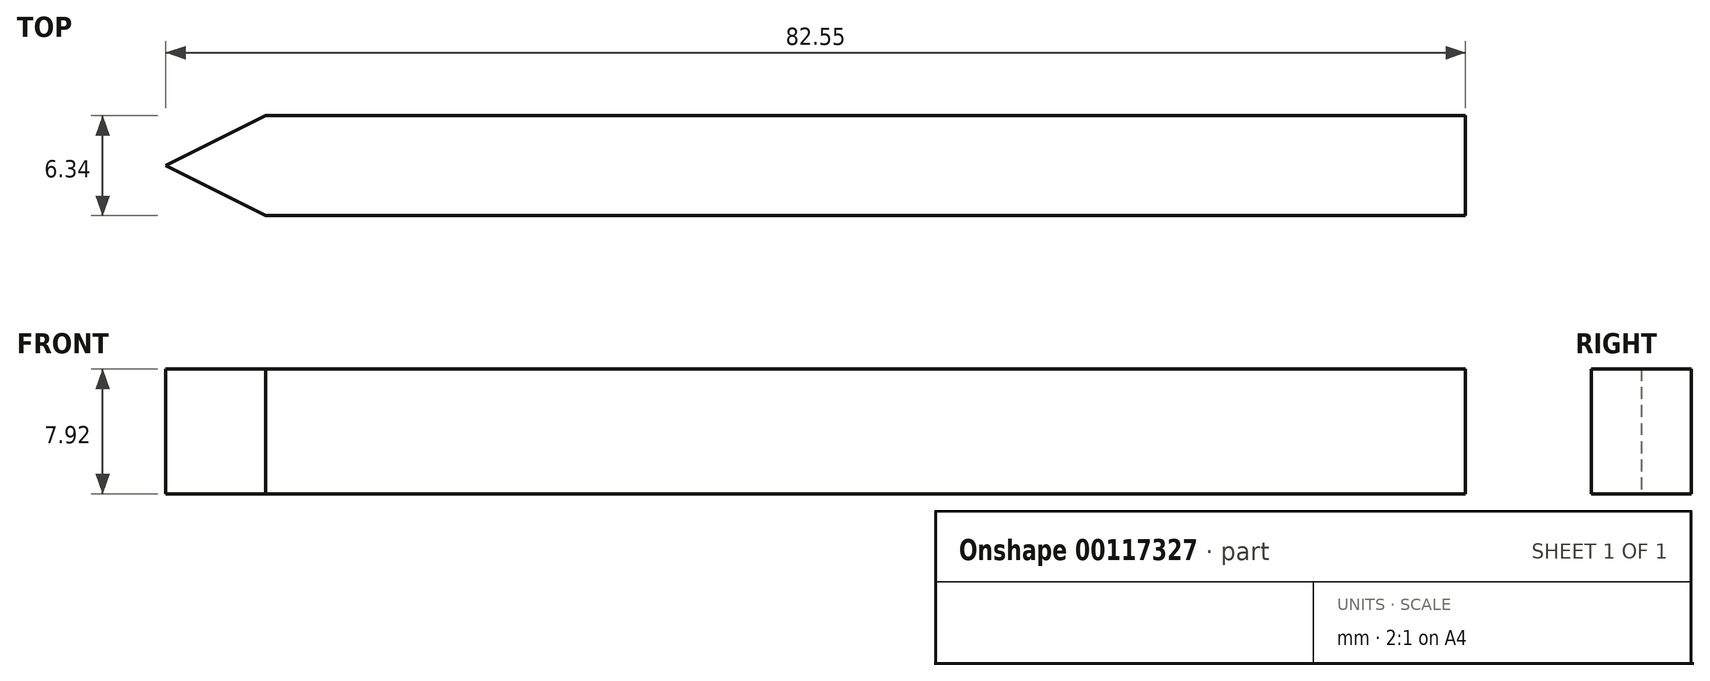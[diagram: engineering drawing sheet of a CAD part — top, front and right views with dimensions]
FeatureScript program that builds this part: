
annotation { "Feature Type Name" : "Feature", "Feature Type Description" : "" }
export const myFeature = defineFeature(function(context is Context, id is Id, definition is map)
    precondition{}
    {
        {
            var Q0;
            Q0=qCreatedBy(makeId("Top.planeOp"),FACE);
            var sketch = newSketch(context, id + "F0", { "sketchPlane" : qUnion([Q0])});
            skLineSegment(sketch, "E0.bottom", {"start": v(38.1, 3.18) * mm, "end": v(-38.1, 3.18) * mm});
            skLineSegment(sketch, "E0.top", {"start": v(38.1, -3.18) * mm, "end": v(-38.1, -3.18) * mm});
            skLineSegment(sketch, "E0.left", {"start": v(38.1, 3.18) * mm, "end": v(38.1, -3.17) * mm});
            skLineSegment(sketch, "E0.right", {"start": v(-38.1, 3.18) * mm, "end": v(-38.1, -3.18) * mm, "construction": true});
            skPoint(sketch, "E0.middle", {"position": v(0, 0) * mm});
            skLineSegment(sketch, "E1", {"start": v(-38.1, 0) * mm, "end": v(-44.45, 0) * mm, "construction": true});
            skLineSegment(sketch, "E2", {"start": v(-38.1, -3.17) * mm, "end": v(-44.45, 0) * mm});
            skLineSegment(sketch, "E3", {"start": v(-38.1, 3.17) * mm, "end": v(-44.45, 0) * mm});
            skSolve(sketch);
        }
        {
            var Q0;
            Q0 = qSketchRegion(id + "F0", true);
            extrude(context, id + "F1", {"entities" : qUnion([Q0]), "depth" : 7.92 * mm});
        }
    });
